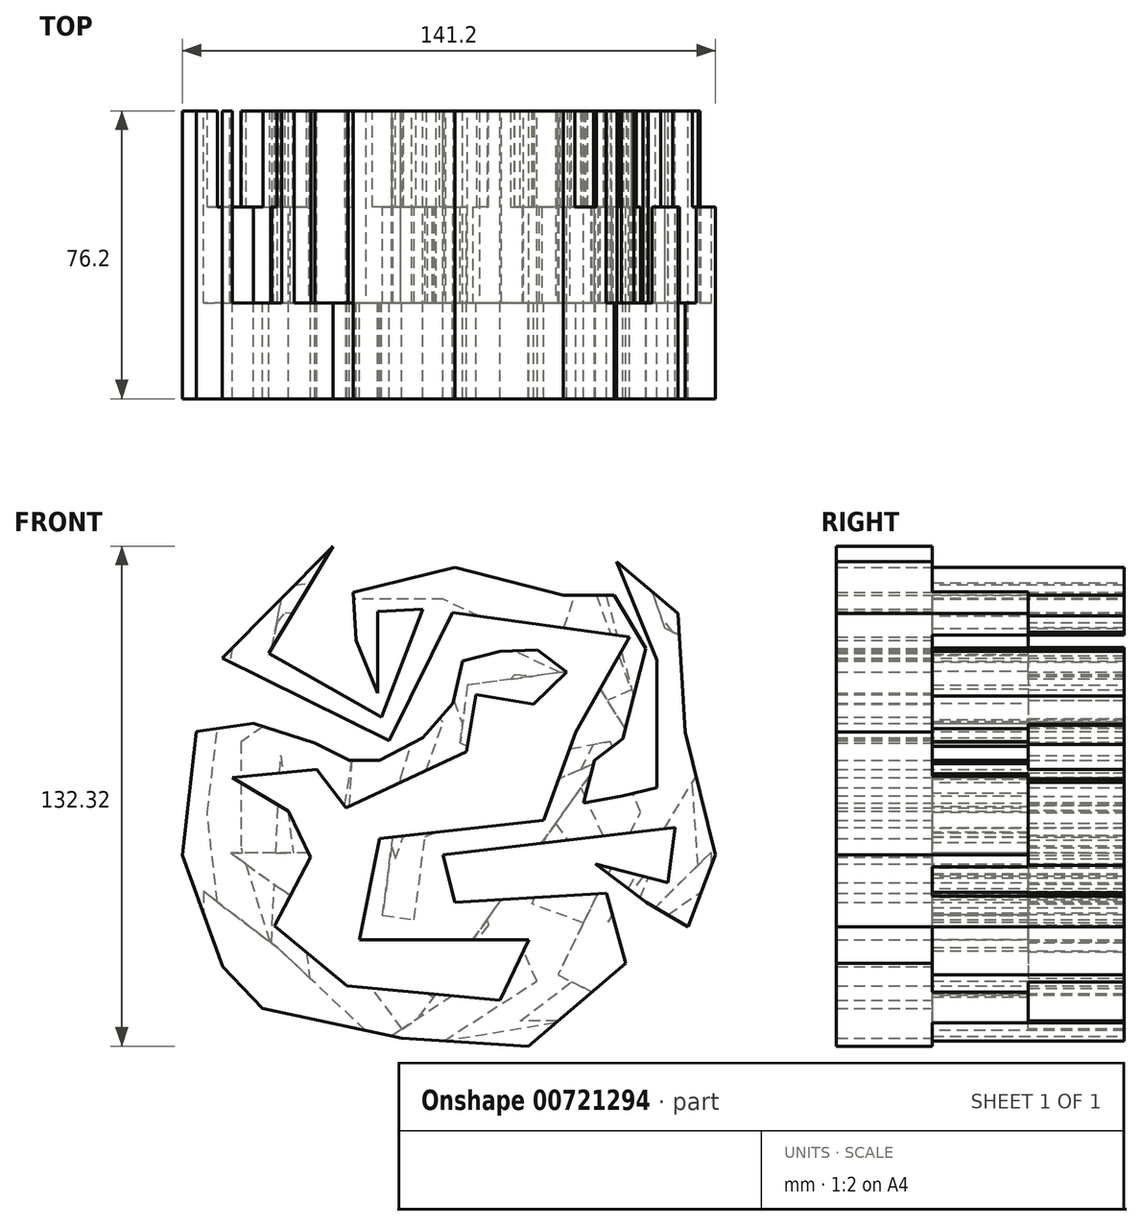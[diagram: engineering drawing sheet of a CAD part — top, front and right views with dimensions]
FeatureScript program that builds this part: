
annotation { "Feature Type Name" : "Feature", "Feature Type Description" : "" }
export const myFeature = defineFeature(function(context is Context, id is Id, definition is map)
    precondition{}
    {
        {
            var Q0;
            Q0=qCreatedBy(makeId("Front.planeOp"),FACE);
            var sketch = newSketch(context, id + "F0", { "sketchPlane" : qUnion([Q0])});
            skLineSegment(sketch, "E0", {"start": v(-29.15, 61.3) * mm, "end": v(-58.5, 31.74) * mm});
            skLineSegment(sketch, "E1", {"start": v(-58.5, 31.74) * mm, "end": v(-14.27, 9.82) * mm});
            skLineSegment(sketch, "E2", {"start": v(-14.27, 9.82) * mm, "end": v(2.52, 43.71) * mm});
            skLineSegment(sketch, "E3", {"start": v(2.52, 43.71) * mm, "end": v(49.41, 37.32) * mm});
            skLineSegment(sketch, "E4", {"start": v(49.41, 37.32) * mm, "end": v(35.15, 12.1) * mm});
            skLineSegment(sketch, "E5", {"start": v(35.15, 12.1) * mm, "end": v(26.67, -11.27) * mm});
            skLineSegment(sketch, "E6", {"start": v(26.67, -11.27) * mm, "end": v(-16.75, -16.02) * mm});
            skLineSegment(sketch, "E7", {"start": v(-16.75, -16.02) * mm, "end": v(-22.12, -42.9) * mm});
            skLineSegment(sketch, "E8", {"start": v(-22.12, -42.9) * mm, "end": v(22.74, -42.9) * mm});
            skLineSegment(sketch, "E9", {"start": v(22.74, -42.9) * mm, "end": v(15.1, -58.82) * mm});
            skLineSegment(sketch, "E10", {"start": v(15.1, -58.82) * mm, "end": v(-25.43, -55.1) * mm});
            skLineSegment(sketch, "E11", {"start": v(-25.43, -55.1) * mm, "end": v(-44.66, -39.18) * mm});
            skLineSegment(sketch, "E12", {"start": v(-44.66, -39.18) * mm, "end": v(-35.15, -20.98) * mm});
            skLineSegment(sketch, "E13", {"start": v(-35.15, -20.98) * mm, "end": v(-40.94, -8.79) * mm});
            skLineSegment(sketch, "E14", {"start": v(-40.94, -8.79) * mm, "end": v(-55.82, 0) * mm});
            skLineSegment(sketch, "E15", {"start": v(-55.82, 0) * mm, "end": v(-33.5, 2.17) * mm});
            skLineSegment(sketch, "E16", {"start": v(-33.5, 2.17) * mm, "end": v(-25.64, -7.96) * mm});
            skLineSegment(sketch, "E17", {"start": v(-25.64, -7.96) * mm, "end": v(6.2, 6.93) * mm});
            skLineSegment(sketch, "E18", {"start": v(6.2, 6.93) * mm, "end": v(8.68, 22.02) * mm});
            skLineSegment(sketch, "E19", {"start": v(8.68, 22.02) * mm, "end": v(24.01, 19.5) * mm});
            skLineSegment(sketch, "E20", {"start": v(24.01, 19.5) * mm, "end": v(32.67, 28.01) * mm});
            skLineSegment(sketch, "E21", {"start": v(32.67, 28.01) * mm, "end": v(25.02, 33.8) * mm});
            skLineSegment(sketch, "E22", {"start": v(25.02, 33.8) * mm, "end": v(15.1, 33.39) * mm});
            skLineSegment(sketch, "E23", {"start": v(15.1, 33.39) * mm, "end": v(5.17, 30.9) * mm});
            skLineSegment(sketch, "E24", {"start": v(5.17, 30.9) * mm, "end": v(2.69, 19.74) * mm});
            skLineSegment(sketch, "E25", {"start": v(2.69, 19.74) * mm, "end": v(-5.38, 10.65) * mm});
            skLineSegment(sketch, "E26", {"start": v(-5.38, 10.65) * mm, "end": v(-16.75, 4.65) * mm});
            skLineSegment(sketch, "E27", {"start": v(-16.75, 4.65) * mm, "end": v(-24.8, 4.65) * mm});
            skLineSegment(sketch, "E28", {"start": v(-24.8, 4.65) * mm, "end": v(-33.9, 9.2) * mm});
            skLineSegment(sketch, "E29", {"start": v(-33.9, 9.2) * mm, "end": v(-50.24, 14.37) * mm});
            skLineSegment(sketch, "E30", {"start": v(-50.24, 14.37) * mm, "end": v(-65.33, 12.3) * mm});
            skLineSegment(sketch, "E31", {"start": v(-65.33, 12.3) * mm, "end": v(-69.05, -20.57) * mm});
            skLineSegment(sketch, "E32", {"start": v(-69.05, -20.57) * mm, "end": v(-58.3, -49.93) * mm});
            skLineSegment(sketch, "E33", {"start": v(-58.3, -49.93) * mm, "end": v(-47.76, -61.1) * mm});
            skLineSegment(sketch, "E34", {"start": v(-47.76, -61.1) * mm, "end": v(-10.96, -68.95) * mm});
            skLineSegment(sketch, "E35", {"start": v(-10.96, -68.95) * mm, "end": v(22.54, -71.02) * mm});
            skLineSegment(sketch, "E36", {"start": v(22.54, -71.02) * mm, "end": v(48.38, -49.1) * mm});
            skLineSegment(sketch, "E37", {"start": v(48.38, -49.1) * mm, "end": v(43.2, -30.5) * mm});
            skLineSegment(sketch, "E38", {"start": v(43.2, -30.5) * mm, "end": v(3.1, -32.98) * mm});
            skLineSegment(sketch, "E39", {"start": v(3.1, -32.98) * mm, "end": v(0, -20.36) * mm});
            skLineSegment(sketch, "E40", {"start": v(0, -20.36) * mm, "end": v(61.4, -13.13) * mm});
            skLineSegment(sketch, "E41", {"start": v(61.4, -13.13) * mm, "end": v(59.54, -27.8) * mm});
            skLineSegment(sketch, "E42", {"start": v(59.54, -27.8) * mm, "end": v(40.32, -22.85) * mm});
            skLineSegment(sketch, "E43", {"start": v(40.32, -22.85) * mm, "end": v(53.75, -32.98) * mm});
            skLineSegment(sketch, "E44", {"start": v(53.75, -32.98) * mm, "end": v(64.92, -39.38) * mm});
            skLineSegment(sketch, "E45", {"start": v(64.92, -39.38) * mm, "end": v(72.15, -20.36) * mm});
            skLineSegment(sketch, "E46", {"start": v(72.15, -20.36) * mm, "end": v(64.16, 12.16) * mm});
            skLineSegment(sketch, "E47", {"start": v(64.16, 12.16) * mm, "end": v(62.22, 43.5) * mm});
            skLineSegment(sketch, "E48", {"start": v(62.22, 43.5) * mm, "end": v(45.9, 57.16) * mm});
            skLineSegment(sketch, "E49", {"start": v(45.9, 57.16) * mm, "end": v(56.65, 31.12) * mm});
            skLineSegment(sketch, "E50", {"start": v(56.65, 31.12) * mm, "end": v(56.65, -2.58) * mm});
            skLineSegment(sketch, "E51", {"start": v(56.65, -2.58) * mm, "end": v(47.55, -4.82) * mm});
            skLineSegment(sketch, "E52", {"start": v(47.55, -4.82) * mm, "end": v(37.21, -6.72) * mm});
            skLineSegment(sketch, "E53", {"start": v(37.21, -6.72) * mm, "end": v(40.13, 4.6) * mm});
            skLineSegment(sketch, "E54", {"start": v(40.13, 4.6) * mm, "end": v(47.58, 10.37) * mm});
            skLineSegment(sketch, "E55", {"start": v(47.58, 10.37) * mm, "end": v(50.63, 22.18) * mm});
            skLineSegment(sketch, "E56", {"start": v(50.63, 22.18) * mm, "end": v(53.73, 34.21) * mm});
            skLineSegment(sketch, "E57", {"start": v(53.73, 34.21) * mm, "end": v(45.28, 48.27) * mm});
            skLineSegment(sketch, "E58", {"start": v(45.28, 48.27) * mm, "end": v(31.84, 48.27) * mm});
            skLineSegment(sketch, "E59", {"start": v(31.84, 48.27) * mm, "end": v(3.1, 55.7) * mm});
            skLineSegment(sketch, "E60", {"start": v(3.1, 55.7) * mm, "end": v(-23.82, 49.07) * mm});
            skLineSegment(sketch, "E61", {"start": v(-23.82, 49.07) * mm, "end": v(-23.04, 36.35) * mm});
            skLineSegment(sketch, "E62", {"start": v(-23.04, 36.35) * mm, "end": v(-17.26, 22.37) * mm});
            skLineSegment(sketch, "E63", {"start": v(-17.26, 22.37) * mm, "end": v(-17.26, 43.93) * mm});
            skLineSegment(sketch, "E64", {"start": v(-17.26, 43.93) * mm, "end": v(-5.37, 44.67) * mm});
            skLineSegment(sketch, "E65", {"start": v(-5.37, 44.67) * mm, "end": v(-16.33, 16.02) * mm});
            skLineSegment(sketch, "E66", {"start": v(-16.33, 16.02) * mm, "end": v(-46.1, 32.98) * mm});
            skLineSegment(sketch, "E67", {"start": v(-46.1, 32.98) * mm, "end": v(-29.15, 61.3) * mm});
            skSolve(sketch);
        }
        {
            var Q0;
            Q0 = qSketchRegion(id + "F0", true);
            extrude(context, id + "F1", {"entities" : qUnion([Q0]), "depth" : 76.2 * mm, "offsetDistance" : 25.4 * mm});
        }
        {
            var Q0;
            Q0=qCreatedBy(makeId("Front.planeOp"),FACE);
            var sketch = newSketch(context, id + "F2", { "sketchPlane" : qUnion([Q0])});
            skLineSegment(sketch, "E68", {"start": v(37.63, 56.13) * mm, "end": v(49.83, 23.26) * mm});
            skLineSegment(sketch, "E69", {"start": v(49.83, 23.26) * mm, "end": v(15.3, 7.75) * mm});
            skLineSegment(sketch, "E70", {"start": v(15.3, 7.75) * mm, "end": v(36.39, -21.2) * mm});
            skLineSegment(sketch, "E71", {"start": v(36.39, -21.2) * mm, "end": v(69.05, -46.2) * mm});
            skLineSegment(sketch, "E72", {"start": v(69.05, -46.2) * mm, "end": v(64.92, 14.58) * mm});
            skLineSegment(sketch, "E73", {"start": v(64.92, 14.58) * mm, "end": v(50.45, 3.82) * mm});
            skLineSegment(sketch, "E74", {"start": v(50.45, 3.82) * mm, "end": v(58.5, -18.71) * mm});
            skLineSegment(sketch, "E75", {"start": v(58.5, -18.71) * mm, "end": v(43.83, -18.71) * mm});
            skLineSegment(sketch, "E76", {"start": v(43.83, -18.71) * mm, "end": v(35.35, 0) * mm});
            skLineSegment(sketch, "E77", {"start": v(35.35, 0) * mm, "end": v(41.35, 11.89) * mm});
            skLineSegment(sketch, "E78", {"start": v(41.35, 11.89) * mm, "end": v(56.85, 16.64) * mm});
            skLineSegment(sketch, "E79", {"start": v(56.85, 16.64) * mm, "end": v(61.82, 37.32) * mm});
            skLineSegment(sketch, "E80", {"start": v(61.82, 37.32) * mm, "end": v(49.83, 53.03) * mm});
            skLineSegment(sketch, "E81", {"start": v(49.83, 53.03) * mm, "end": v(63.47, 53.03) * mm});
            skLineSegment(sketch, "E82", {"start": v(63.47, 53.03) * mm, "end": v(68.64, 25.95) * mm});
            skLineSegment(sketch, "E83", {"start": v(68.64, 25.95) * mm, "end": v(73.19, 0) * mm});
            skLineSegment(sketch, "E84", {"start": v(73.19, 0) * mm, "end": v(73.19, -64.4) * mm});
            skLineSegment(sketch, "E85", {"start": v(73.19, -64.4) * mm, "end": v(20.47, -64.4) * mm});
            skLineSegment(sketch, "E86", {"start": v(20.47, -64.4) * mm, "end": v(40.73, -48.9) * mm});
            skLineSegment(sketch, "E87", {"start": v(40.73, -48.9) * mm, "end": v(58.72, -53.03) * mm});
            skLineSegment(sketch, "E88", {"start": v(58.72, -53.03) * mm, "end": v(42.59, -56.96) * mm});
            skLineSegment(sketch, "E89", {"start": v(42.59, -56.96) * mm, "end": v(68.02, -59.44) * mm});
            skLineSegment(sketch, "E90", {"start": v(68.02, -59.44) * mm, "end": v(68.02, -49.93) * mm});
            skLineSegment(sketch, "E91", {"start": v(68.02, -49.93) * mm, "end": v(23.57, -33.39) * mm});
            skLineSegment(sketch, "E92", {"start": v(23.57, -33.39) * mm, "end": v(26.51, -25.47) * mm});
            skLineSegment(sketch, "E93", {"start": v(26.51, -25.47) * mm, "end": v(3.93, -9.61) * mm});
            skLineSegment(sketch, "E94", {"start": v(3.93, -9.61) * mm, "end": v(12, -38.97) * mm});
            skLineSegment(sketch, "E95", {"start": v(12, -38.97) * mm, "end": v(-9.92, -67.7) * mm});
            skLineSegment(sketch, "E96", {"start": v(-9.92, -67.7) * mm, "end": v(-31.22, -38.76) * mm});
            skLineSegment(sketch, "E97", {"start": v(-31.22, -38.76) * mm, "end": v(-22.74, 12.92) * mm});
            skLineSegment(sketch, "E98", {"start": v(-22.74, 12.92) * mm, "end": v(-12.61, -21.4) * mm});
            skLineSegment(sketch, "E99", {"start": v(-12.61, -21.4) * mm, "end": v(0, 14.78) * mm});
            skLineSegment(sketch, "E100", {"start": v(0, 14.78) * mm, "end": v(-18.6, 33.8) * mm});
            skLineSegment(sketch, "E101", {"start": v(-18.6, 33.8) * mm, "end": v(-53.55, 9.4) * mm});
            skLineSegment(sketch, "E102", {"start": v(-53.55, 9.4) * mm, "end": v(-53.55, -18.5) * mm});
            skLineSegment(sketch, "E103", {"start": v(-53.55, -18.5) * mm, "end": v(-45.48, -44.76) * mm});
            skLineSegment(sketch, "E104", {"start": v(-45.48, -44.76) * mm, "end": v(-43, 5.9) * mm});
            skLineSegment(sketch, "E105", {"start": v(-43, 5.9) * mm, "end": v(-34.73, -57.16) * mm});
            skLineSegment(sketch, "E106", {"start": v(-34.73, -57.16) * mm, "end": v(-48.41, -58.96) * mm});
            skLineSegment(sketch, "E107", {"start": v(-48.41, -58.96) * mm, "end": v(-59.34, -36.7) * mm});
            skLineSegment(sketch, "E108", {"start": v(-59.34, -36.7) * mm, "end": v(-62.44, -9.2) * mm});
            skLineSegment(sketch, "E109", {"start": v(-62.44, -9.2) * mm, "end": v(-59.34, 15.82) * mm});
            skLineSegment(sketch, "E110", {"start": v(-59.34, 15.82) * mm, "end": v(-48.58, 35.46) * mm});
            skLineSegment(sketch, "E111", {"start": v(-48.58, 35.46) * mm, "end": v(-41.76, 43.73) * mm});
            skLineSegment(sketch, "E112", {"start": v(-41.76, 43.73) * mm, "end": v(-19.85, 41.87) * mm});
            skLineSegment(sketch, "E113", {"start": v(-19.85, 41.87) * mm, "end": v(-5.38, 41.87) * mm});
            skLineSegment(sketch, "E114", {"start": v(-5.38, 41.87) * mm, "end": v(6, 12.1) * mm});
            skLineSegment(sketch, "E115", {"start": v(6, 12.1) * mm, "end": v(19.02, 27.4) * mm});
            skLineSegment(sketch, "E116", {"start": v(19.02, 27.4) * mm, "end": v(35.97, 25.53) * mm});
            skLineSegment(sketch, "E117", {"start": v(35.97, 25.53) * mm, "end": v(7.65, 38.76) * mm});
            skLineSegment(sketch, "E118", {"start": v(7.65, 38.76) * mm, "end": v(31.63, 38.76) * mm});
            skLineSegment(sketch, "E119", {"start": v(31.63, 38.76) * mm, "end": v(37.63, 56.13) * mm});
            skSolve(sketch);
        }
        {
            var Q0;
            Q0 = qSketchRegion(id + "F2", true);
            extrude(context, id + "F3", {"entities" : qUnion([Q0]), "operationType" : NewBodyOperationType.REMOVE, "oppositeDirection" : true, "depth" : -25.4 * mm, "offsetDistance" : 25.4 * mm});
        }
        {
            var Q0;
            Q0=qCreatedBy(makeId("Front.planeOp"),FACE);
            var sketch = newSketch(context, id + "F4", { "sketchPlane" : qUnion([Q0])});
            skLineSegment(sketch, "E120", {"start": v(-51.9, 57.58) * mm, "end": v(-58.1, 20.78) * mm});
            skLineSegment(sketch, "E121", {"start": v(-58.1, 20.78) * mm, "end": v(-23.5, 14.95) * mm});
            skLineSegment(sketch, "E122", {"start": v(-23.5, 14.95) * mm, "end": v(-25.43, -19.95) * mm});
            skLineSegment(sketch, "E123", {"start": v(-25.43, -19.95) * mm, "end": v(-56.23, -19.95) * mm});
            skLineSegment(sketch, "E124", {"start": v(-56.23, -19.95) * mm, "end": v(-2.9, -58) * mm});
            skLineSegment(sketch, "E125", {"start": v(-2.9, -58) * mm, "end": v(41.65, 4.47) * mm});
            skLineSegment(sketch, "E126", {"start": v(41.65, 4.47) * mm, "end": v(-4.76, -15.6) * mm});
            skLineSegment(sketch, "E127", {"start": v(-4.76, -15.6) * mm, "end": v(-7.65, -37.52) * mm});
            skLineSegment(sketch, "E128", {"start": v(-7.65, -37.52) * mm, "end": v(-16.02, -36.42) * mm});
            skLineSegment(sketch, "E129", {"start": v(-16.02, -36.42) * mm, "end": v(-11.2, 0) * mm});
            skLineSegment(sketch, "E130", {"start": v(-11.2, 0) * mm, "end": v(0, 34.63) * mm});
            skLineSegment(sketch, "E131", {"start": v(0, 34.63) * mm, "end": v(30.18, 33.18) * mm});
            skLineSegment(sketch, "E132", {"start": v(30.18, 33.18) * mm, "end": v(0, 47.24) * mm});
            skLineSegment(sketch, "E133", {"start": v(0, 47.24) * mm, "end": v(-26.46, 47.24) * mm});
            skLineSegment(sketch, "E134", {"start": v(-26.46, 47.24) * mm, "end": v(-33.29, 32.36) * mm});
            skLineSegment(sketch, "E135", {"start": v(-33.29, 32.36) * mm, "end": v(-45.7, 32.36) * mm});
            skLineSegment(sketch, "E136", {"start": v(-45.7, 32.36) * mm, "end": v(-42.18, 50.55) * mm});
            skLineSegment(sketch, "E137", {"start": v(-42.18, 50.55) * mm, "end": v(12.2, 58.2) * mm});
            skLineSegment(sketch, "E138", {"start": v(12.2, 58.2) * mm, "end": v(42.18, 51.79) * mm});
            skLineSegment(sketch, "E139", {"start": v(42.18, 51.79) * mm, "end": v(56.44, 0) * mm});
            skLineSegment(sketch, "E140", {"start": v(56.44, 0) * mm, "end": v(38.25, 28.84) * mm});
            skLineSegment(sketch, "E141", {"start": v(38.25, 28.84) * mm, "end": v(6.4, 24.5) * mm});
            skLineSegment(sketch, "E142", {"start": v(6.4, 24.5) * mm, "end": v(4.55, 9.2) * mm});
            skLineSegment(sketch, "E143", {"start": v(4.55, 9.2) * mm, "end": v(14.68, 4.47) * mm});
            skLineSegment(sketch, "E144", {"start": v(14.68, 4.47) * mm, "end": v(14.68, 16.64) * mm});
            skLineSegment(sketch, "E145", {"start": v(14.68, 16.64) * mm, "end": v(28.74, 14.78) * mm});
            skLineSegment(sketch, "E146", {"start": v(28.74, 14.78) * mm, "end": v(27.66, 6.62) * mm});
            skLineSegment(sketch, "E147", {"start": v(27.66, 6.62) * mm, "end": v(44.24, 9.61) * mm});
            skLineSegment(sketch, "E148", {"start": v(44.24, 9.61) * mm, "end": v(52.35, -9.12) * mm});
            skLineSegment(sketch, "E149", {"start": v(52.35, -9.12) * mm, "end": v(41.65, -29.25) * mm});
            skLineSegment(sketch, "E150", {"start": v(41.65, -29.25) * mm, "end": v(30.4, -52.2) * mm});
            skLineSegment(sketch, "E151", {"start": v(30.4, -52.2) * mm, "end": v(41.65, -57.73) * mm});
            skLineSegment(sketch, "E152", {"start": v(41.65, -57.73) * mm, "end": v(59.13, -36.5) * mm});
            skLineSegment(sketch, "E153", {"start": v(59.13, -36.5) * mm, "end": v(68.23, -30.29) * mm});
            skLineSegment(sketch, "E154", {"start": v(68.23, -30.29) * mm, "end": v(61.2, -59.85) * mm});
            skLineSegment(sketch, "E155", {"start": v(61.2, -59.85) * mm, "end": v(32.67, -64.4) * mm});
            skLineSegment(sketch, "E156", {"start": v(32.67, -64.4) * mm, "end": v(0, -69.78) * mm});
            skLineSegment(sketch, "E157", {"start": v(0, -69.78) * mm, "end": v(24.8, -53.86) * mm});
            skLineSegment(sketch, "E158", {"start": v(24.8, -53.86) * mm, "end": v(21.17, -45.44) * mm});
            skLineSegment(sketch, "E159", {"start": v(21.17, -45.44) * mm, "end": v(-16.75, -70.4) * mm});
            skLineSegment(sketch, "E160", {"start": v(-16.75, -70.4) * mm, "end": v(-43.83, -44.97) * mm});
            skLineSegment(sketch, "E161", {"start": v(-43.83, -44.97) * mm, "end": v(-63.47, -30.08) * mm});
            skLineSegment(sketch, "E162", {"start": v(-63.47, -30.08) * mm, "end": v(-63.47, -58) * mm});
            skLineSegment(sketch, "E163", {"start": v(-63.47, -58) * mm, "end": v(-38.04, -73.3) * mm});
            skLineSegment(sketch, "E164", {"start": v(-38.04, -73.3) * mm, "end": v(56.44, -73.3) * mm});
            skLineSegment(sketch, "E165", {"start": v(56.44, -73.3) * mm, "end": v(70.91, -53.86) * mm});
            skLineSegment(sketch, "E166", {"start": v(70.91, -53.86) * mm, "end": v(70.91, -19.74) * mm});
            skLineSegment(sketch, "E167", {"start": v(70.91, -19.74) * mm, "end": v(47.34, -43.1) * mm});
            skLineSegment(sketch, "E168", {"start": v(47.34, -43.1) * mm, "end": v(56.44, -21.6) * mm});
            skLineSegment(sketch, "E169", {"start": v(56.44, -21.6) * mm, "end": v(43.62, -38.14) * mm});
            skLineSegment(sketch, "E170", {"start": v(43.62, -38.14) * mm, "end": v(69.47, 4.47) * mm});
            skLineSegment(sketch, "E171", {"start": v(69.47, 4.47) * mm, "end": v(66.57, 35.87) * mm});
            skLineSegment(sketch, "E172", {"start": v(66.57, 35.87) * mm, "end": v(58.72, 39.6) * mm});
            skLineSegment(sketch, "E173", {"start": v(58.72, 39.6) * mm, "end": v(50.45, 63.37) * mm});
            skLineSegment(sketch, "E174", {"start": v(50.45, 63.37) * mm, "end": v(28.12, 66.26) * mm});
            skLineSegment(sketch, "E175", {"start": v(28.12, 66.26) * mm, "end": v(-4.34, 66.26) * mm});
            skLineSegment(sketch, "E176", {"start": v(-4.34, 66.26) * mm, "end": v(-27.3, 63.57) * mm});
            skLineSegment(sketch, "E177", {"start": v(-27.3, 63.57) * mm, "end": v(-51.9, 57.58) * mm});
            skSolve(sketch);
        }
        {
            var Q0;
            Q0 = qSketchRegion(id + "F4", true);
            extrude(context, id + "F5", {"entities" : qUnion([Q0]), "operationType" : NewBodyOperationType.REMOVE, "oppositeDirection" : true, "depth" : -50.8 * mm, "offsetDistance" : 25.4 * mm});
        }
    });
